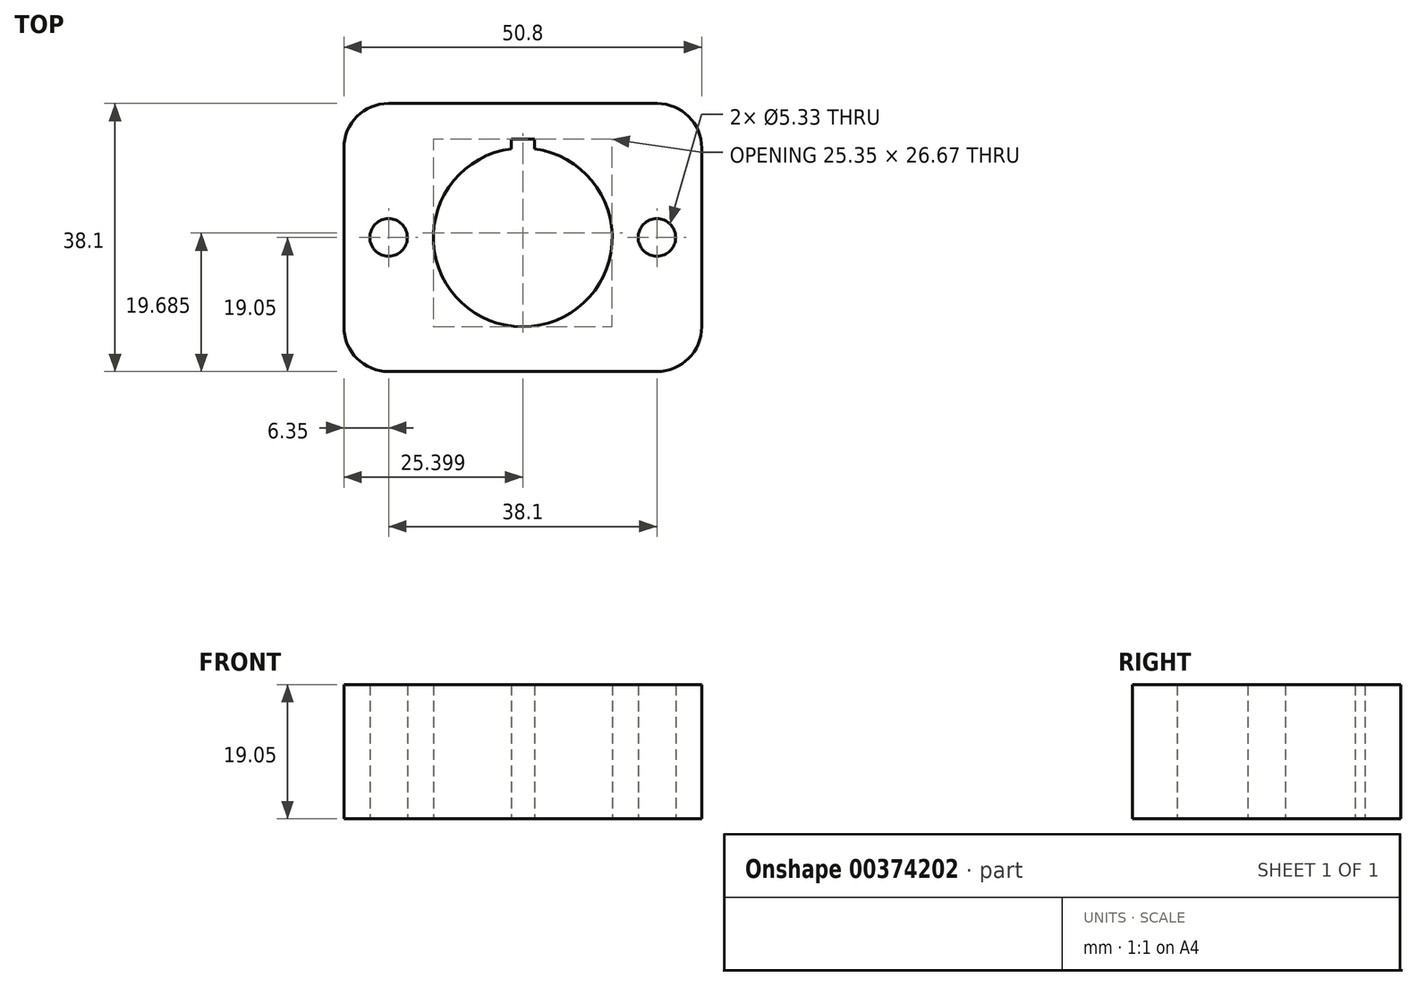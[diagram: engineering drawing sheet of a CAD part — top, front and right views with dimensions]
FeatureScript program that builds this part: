
annotation { "Feature Type Name" : "Feature", "Feature Type Description" : "" }
export const myFeature = defineFeature(function(context is Context, id is Id, definition is map)
    precondition{}
    {
        {
            var Q0;
            Q0=qCreatedBy(makeId("Top.planeOp"),FACE);
            var sketch = newSketch(context, id + "F0", { "sketchPlane" : qUnion([Q0])});
            skLineSegment(sketch, "E0.bottom", {"start": v(19.05, 19.05) * mm, "end": v(-19.05, 19.05) * mm});
            skLineSegment(sketch, "E0.top", {"start": v(19.05, -19.05) * mm, "end": v(-19.05, -19.05) * mm});
            skLineSegment(sketch, "E0.left", {"start": v(25.4, 12.7) * mm, "end": v(25.4, -12.7) * mm});
            skLineSegment(sketch, "E0.right", {"start": v(-25.4, 12.7) * mm, "end": v(-25.4, -12.7) * mm});
            skPoint(sketch, "E0.middle", {"position": v(0, 0) * mm});
            skCircle(sketch, "E1", {"center": v(0, 0) * mm, "radius": 12.7 * mm});
            skCircle(sketch, "E2", {"center": v(19.05, 0) * mm, "radius": 2.67 * mm});
            skCircle(sketch, "E3", {"center": v(-19.05, 0) * mm, "radius": 2.67 * mm});
            skPoint(sketch, "E4.visualSharp", {"position": v(-25.4, 19.05) * mm});
            skArc(sketch, "E4.filletArc", {"start": v(-19.05, 19.05) * mm, "mid": v(-23.54, 17.2) * mm, "end": v(-25.4, 12.7) * mm});
            skPoint(sketch, "E5.visualSharp", {"position": v(25.4, 19.05) * mm});
            skArc(sketch, "E5.filletArc", {"start": v(25.4, 12.7) * mm, "mid": v(23.54, 17.2) * mm, "end": v(19.05, 19.05) * mm});
            skPoint(sketch, "E6.visualSharp", {"position": v(25.4, -19.05) * mm});
            skArc(sketch, "E6.filletArc", {"start": v(19.05, -19.05) * mm, "mid": v(23.54, -17.2) * mm, "end": v(25.4, -12.7) * mm});
            skPoint(sketch, "E7.visualSharp", {"position": v(-25.4, -19.05) * mm});
            skArc(sketch, "E7.filletArc", {"start": v(-25.4, -12.7) * mm, "mid": v(-23.54, -17.2) * mm, "end": v(-19.05, -19.05) * mm});
            skLineSegment(sketch, "E8.left", {"start": v(0.01, 15.24) * mm, "end": v(0.01, 12.7) * mm});
            skPoint(sketch, "E8.middle", {"position": v(0, 12.7) * mm});
            skLineSegment(sketch, "E9", {"start": v(0, 15.05) * mm, "end": v(0, 7.48) * mm, "construction": true});
            skLineSegment(sketch, "E10.bottom", {"start": v(1.66, 13.97) * mm, "end": v(-1.64, 13.97) * mm});
            skLineSegment(sketch, "E10.left", {"start": v(1.66, 13.97) * mm, "end": v(1.66, 12.6) * mm});
            skLineSegment(sketch, "E10.right", {"start": v(-1.64, 13.97) * mm, "end": v(-1.64, 12.6) * mm});
            skPoint(sketch, "E10.middle", {"position": v(0.01, 12.7) * mm});
            skPoint(sketch, "E10.cornerSnap0", {"position": v(0.01, 13.97) * mm});
            skSolve(sketch);
        }
        {
            var Q0;
            Q0 = qSketchRegion(id + "F0", true);
            extrude(context, id + "F1", {"entities" : qUnion([Q0]), "depth" : 19.05 * mm});
        }
    });
